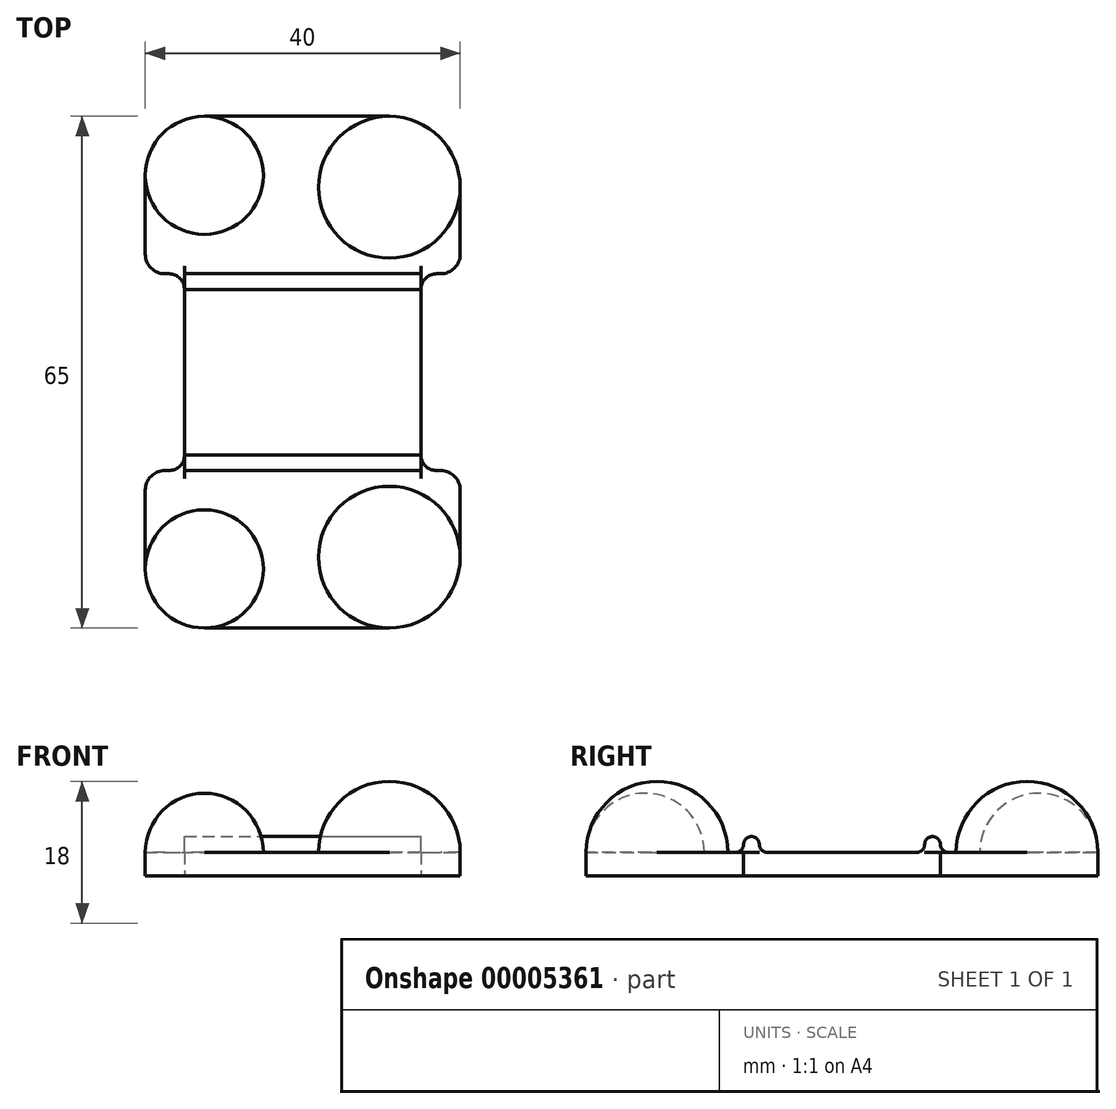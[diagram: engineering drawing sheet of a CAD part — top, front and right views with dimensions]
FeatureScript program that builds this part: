
annotation { "Feature Type Name" : "Feature", "Feature Type Description" : "" }
export const myFeature = defineFeature(function(context is Context, id is Id, definition is map)
    precondition{}
    {
        {
            var Q0;
            Q0=qCreatedBy(makeId("Top.planeOp"),FACE);
            var sketch = newSketch(context, id + "F0", { "sketchPlane" : qUnion([Q0])});
            skLineSegment(sketch, "E0.rect.bottom", {"start": v(20, 32.5) * mm, "end": v(-20, 32.5) * mm});
            skLineSegment(sketch, "E0.rect.top", {"start": v(20, -32.5) * mm, "end": v(-20, -32.5) * mm});
            skLineSegment(sketch, "E0.rect.left", {"start": v(20, 32.5) * mm, "end": v(20, -32.5) * mm});
            skLineSegment(sketch, "E0.rect.right", {"start": v(-20, 32.5) * mm, "end": v(-20, -32.5) * mm});
            skPoint(sketch, "E0.rect.middle", {"position": v(0, 0) * mm});
            skLineSegment(sketch, "E1", {"start": v(-20, 10.5) * mm, "end": v(20, 10.5) * mm});
            skLineSegment(sketch, "E2", {"start": v(-20, 12.5) * mm, "end": v(20, 12.5) * mm});
            skLineSegment(sketch, "E3", {"start": v(-20, -10.5) * mm, "end": v(20, -10.5) * mm});
            skLineSegment(sketch, "E4", {"start": v(-20, -12.5) * mm, "end": v(20, -12.5) * mm});
            skLineSegment(sketch, "E5", {"start": v(-15, 12.5) * mm, "end": v(-15, -12.5) * mm});
            skLineSegment(sketch, "E6", {"start": v(15, 12.5) * mm, "end": v(15, -12.5) * mm});
            skSolve(sketch);
        }
        {
            var Q0;
            Q0=makeQuery(id+"F0.imprint","IMPRINT",FACE,{"disambiguationData":[TD([[makeQuery(id+"F0.imprint","IMPRINT",EDGE,{"derivedFrom":sQuery(id+"F0.wireOp",EDGE,"E0.rect.bottom")}),1.0]])]});
            var Q1;
            Q1=makeQuery(id+"F0.imprint","IMPRINT",FACE,{"disambiguationData":[TD([[makeQuery(id+"F0.imprint","IMPRINT",EDGE,{"derivedFrom":sQuery(id+"F0.wireOp",EDGE,"bcf83515-ba27-4b76-bd59-bfaced73eee4.0")}),1.0]])]});
            var Q2;
            Q2=makeQuery(id+"F0.imprint","IMPRINT",FACE,{"disambiguationData":[TD([[makeQuery(id+"F0.imprint","IMPRINT",EDGE,{"derivedFrom":sQuery(id+"F0.wireOp",EDGE,"f3534231-453a-4a65-ba47-b9244893f894.bottom")}),1.0]])]});
            var Q3;
            Q3=makeQuery(id+"F0.imprint","IMPRINT",FACE,{"disambiguationData":[TD([[makeQuery(id+"F0.imprint","IMPRINT",EDGE,{"derivedFrom":sQuery(id+"F0.wireOp",EDGE,"e6d423b5-386a-40f2-9fc6-510d5bb70e3d.right")}),-1.0]])]});
            var Q4;
            Q4=makeQuery(id+"F0.imprint","IMPRINT",FACE,{"disambiguationData":[TD([[makeQuery(id+"F0.imprint","IMPRINT",EDGE,{"derivedFrom":sQuery(id+"F0.wireOp",EDGE,"a5c94823-2199-42b4-8307-fa219b560c5c0.MirrorCS")}),1.0]])]});
            var Q5;
            {var subQ2=sQuery(id+"F0.wireOp",EDGE,"E0.rect.top");Q5=makeQuery(id+"F0.imprint","IMPRINT",FACE,{"disambiguationData":[TD([[makeQuery(id+"F0.imprint","IMPRINT",EDGE,{"derivedFrom":subQ2}),-1.0]])]});}
            var Q6;
            {var subQ0=sQuery(id+"F0.wireOp",EDGE,"E5");var subQ1=sQuery(id+"F0.wireOp",EDGE,"E3");var subQ2=makeQuery(id+"F0.imprint","INTERSECT",VERTEX,{"derivedFrom":[subQ1,subQ0]});Q6=makeQuery(id+"F0.imprint","IMPRINT",FACE,{"disambiguationData":[TD([[makeQuery(id+"F0.imprint","IMPRINT",EDGE,{"disambiguationData":[TD([[subQ2,-1.0]])],"derivedFrom":subQ1}),-1.0]])]});}
            var Q7;
            {var subQ0=sQuery(id+"F0.wireOp",EDGE,"E5");var subQ1=sQuery(id+"F0.wireOp",EDGE,"E1");var subQ2=makeQuery(id+"F0.imprint","INTERSECT",VERTEX,{"derivedFrom":[subQ1,subQ0]});Q7=makeQuery(id+"F0.imprint","IMPRINT",FACE,{"disambiguationData":[TD([[makeQuery(id+"F0.imprint","IMPRINT",EDGE,{"disambiguationData":[TD([[subQ2,-1.0]])],"derivedFrom":subQ1}),-1.0]])]});}
            var Q8;
            {var subQ0=sQuery(id+"F0.wireOp",EDGE,"E5");var subQ1=sQuery(id+"F0.wireOp",EDGE,"E1");var subQ2=makeQuery(id+"F0.imprint","INTERSECT",VERTEX,{"derivedFrom":[subQ1,subQ0]});Q8=makeQuery(id+"F0.imprint","IMPRINT",FACE,{"disambiguationData":[TD([[makeQuery(id+"F0.imprint","IMPRINT",EDGE,{"disambiguationData":[TD([[subQ2,-1.0]])],"derivedFrom":subQ1}),1.0]])]});}
            extrude(context, id + "F1", {"entities" : qUnion([Q0, Q1, Q2, Q3, Q4, Q5, Q6, Q7, Q8]), "depth" : 3 * mm});
        }
        {
            var Q0;
            Q0=makeQuery(id+"F1.opExtrude","CAP_FACE",FACE,{"disambiguationData":[OSD([sQuery(id+"F0.wireOp",EDGE,"E0.rect.bottom"),sQuery(id+"F0.wireOp",EDGE,"E0.rect.top"),sQuery(id+"F0.wireOp",EDGE,"E0.rect.left"),sQuery(id+"F0.wireOp",EDGE,"E0.rect.right")])],"isStart":false});
            var sketch = newSketch(context, id + "F2", { "sketchPlane" : qUnion([Q0])});
            skCircle(sketch, "E7", {"center": v(-12.5, 25) * mm, "radius": 7.5 * mm});
            skLineSegment(sketch, "E8", {"start": v(-12.5, 32.5) * mm, "end": v(-12.5, 17.5) * mm});
            skCircle(sketch, "E9", {"center": v(11, 23.5) * mm, "radius": 9 * mm});
            skCircle(sketch, "E10", {"center": v(-12.5, -25) * mm, "radius": 7.5 * mm});
            skCircle(sketch, "E11", {"center": v(11, -23.5) * mm, "radius": 9 * mm});
            skLineSegment(sketch, "E12", {"start": v(-12.5, -17.5) * mm, "end": v(-12.5, -32.5) * mm});
            skLineSegment(sketch, "E13", {"start": v(11, -14.5) * mm, "end": v(11, -32.5) * mm});
            skLineSegment(sketch, "E14", {"start": v(11, 14.5) * mm, "end": v(11, 32.5) * mm});
            skSolve(sketch);
        }
        {
            var Q0;
            {var subQ0=sQuery(id+"F2.wireOp",EDGE,"E8");Q0=makeQuery(id+"F2.imprint","IMPRINT",FACE,{"disambiguationData":[TD([[makeQuery(id+"F2.imprint","IMPRINT",EDGE,{"derivedFrom":subQ0}),-1.0]])]});}
            var Q1;
            Q1=sQuery(id+"F2.wireOp",EDGE,"E8");
            revolve(context, id + "F3", {"operationType" : NewBodyOperationType.ADD, "entities" : qUnion([Q0]), "axis" : qUnion([Q1]), "revolveType" : RevolveType.ONE_DIRECTION, "oppositeDirection" : true, "angle" : 180 * degree});
        }
        {
            var Q0;
            {var subQ0=sQuery(id+"F2.wireOp",EDGE,"E14");Q0=makeQuery(id+"F2.imprint","IMPRINT",FACE,{"disambiguationData":[TD([[makeQuery(id+"F2.imprint","IMPRINT",EDGE,{"derivedFrom":subQ0}),1.0]])]});}
            var Q1;
            Q1=sQuery(id+"F2.wireOp",EDGE,"E14");
            revolve(context, id + "F4", {"operationType" : NewBodyOperationType.ADD, "entities" : qUnion([Q0]), "axis" : qUnion([Q1]), "revolveType" : RevolveType.ONE_DIRECTION, "angle" : 180 * degree});
        }
        {
            var Q0;
            {var subQ0=sQuery(id+"F2.wireOp",EDGE,"E12");Q0=makeQuery(id+"F2.imprint","IMPRINT",FACE,{"disambiguationData":[TD([[makeQuery(id+"F2.imprint","IMPRINT",EDGE,{"derivedFrom":subQ0}),-1.0]])]});}
            var Q1;
            Q1=sQuery(id+"F2.wireOp",EDGE,"E12");
            revolve(context, id + "F5", {"operationType" : NewBodyOperationType.ADD, "entities" : qUnion([Q0]), "axis" : qUnion([Q1]), "revolveType" : RevolveType.ONE_DIRECTION, "oppositeDirection" : true, "angle" : 180 * degree});
        }
        {
            var Q0;
            {var subQ0=sQuery(id+"F2.wireOp",EDGE,"E13");Q0=makeQuery(id+"F2.imprint","IMPRINT",FACE,{"disambiguationData":[TD([[makeQuery(id+"F2.imprint","IMPRINT",EDGE,{"derivedFrom":subQ0}),-1.0]])]});}
            var Q1;
            Q1=sQuery(id+"F2.wireOp",EDGE,"E13");
            revolve(context, id + "F6", {"operationType" : NewBodyOperationType.ADD, "entities" : qUnion([Q0]), "axis" : qUnion([Q1]), "revolveType" : RevolveType.ONE_DIRECTION, "oppositeDirection" : true, "angle" : 180 * degree});
        }
        {
            var Q0;
            {var subQ0=sQuery(id+"F2.wireOp",EDGE,"E11");var subQ1=sQuery(id+"F0.wireOp",EDGE,"E0.rect.top");var subQ2=makeQuery(id+"F1.opExtrude","CAP_EDGE",EDGE,{"disambiguationData":[OSD([subQ1])],"isStart":false});var subQ3=makeQuery(id+"F2.imprint","INTERSECT",VERTEX,{"derivedFrom":[subQ2,subQ0,sQuery(id+"F2.wireOp",EDGE,"E13")]});Q0=makeQuery(id+"F2.imprint","IMPRINT",FACE,{"disambiguationData":[TD([[makeQuery(id+"F2.imprint","IMPRINT",EDGE,{"disambiguationData":[TD([[subQ3,-1.0]])],"derivedFrom":subQ0}),-1.0]])]});}
            var Q1;
            {var subQ0=sQuery(id+"F2.wireOp",EDGE,"E10");var subQ1=sQuery(id+"F0.wireOp",EDGE,"E0.rect.top");var subQ2=makeQuery(id+"F1.opExtrude","CAP_EDGE",EDGE,{"disambiguationData":[OSD([subQ1])],"isStart":false});var subQ3=makeQuery(id+"F2.imprint","INTERSECT",VERTEX,{"derivedFrom":[subQ2,subQ0,sQuery(id+"F2.wireOp",EDGE,"E12")]});Q1=makeQuery(id+"F2.imprint","IMPRINT",FACE,{"disambiguationData":[TD([[makeQuery(id+"F2.imprint","IMPRINT",EDGE,{"disambiguationData":[TD([[subQ3,1.0]])],"derivedFrom":subQ0}),-1.0]])]});}
            var Q2;
            {var subQ0=sQuery(id+"F2.wireOp",EDGE,"E7");var subQ1=sQuery(id+"F0.wireOp",EDGE,"E0.rect.bottom");var subQ2=makeQuery(id+"F1.opExtrude","CAP_EDGE",EDGE,{"disambiguationData":[OSD([subQ1])],"isStart":false});var subQ3=makeQuery(id+"F2.imprint","INTERSECT",VERTEX,{"derivedFrom":[subQ2,sQuery(id+"F2.wireOp",EDGE,"E8"),subQ0]});Q2=makeQuery(id+"F2.imprint","IMPRINT",FACE,{"disambiguationData":[TD([[makeQuery(id+"F2.imprint","IMPRINT",EDGE,{"disambiguationData":[TD([[subQ3,-1.0]])],"derivedFrom":subQ0}),-1.0]])]});}
            var Q3;
            {var subQ0=sQuery(id+"F2.wireOp",EDGE,"E9");var subQ1=sQuery(id+"F0.wireOp",EDGE,"E0.rect.bottom");var subQ2=makeQuery(id+"F1.opExtrude","CAP_EDGE",EDGE,{"disambiguationData":[OSD([subQ1])],"isStart":false});var subQ3=makeQuery(id+"F2.imprint","INTERSECT",VERTEX,{"derivedFrom":[subQ2,subQ0,sQuery(id+"F2.wireOp",EDGE,"E14")]});Q3=makeQuery(id+"F2.imprint","IMPRINT",FACE,{"disambiguationData":[TD([[makeQuery(id+"F2.imprint","IMPRINT",EDGE,{"disambiguationData":[TD([[subQ3,1.0]])],"derivedFrom":subQ0}),-1.0]])]});}
            extrude(context, id + "F7", {"entities" : qUnion([Q0, Q1, Q2, Q3]), "operationType" : NewBodyOperationType.REMOVE, "oppositeDirection" : true, "depth" : 5 * mm});
        }
        {
            var Q0;
            Q0=makeQuery(id+"F1.opExtrude","SWEPT_EDGE",EDGE,{"disambiguationData":[OSD([sQuery(id+"F0.wireOp",EDGE,"E0.rect.left"),sQuery(id+"F0.wireOp",EDGE,"a298e613-06a3-4d8a-99ce-b2c4759a3d300.MirrorCS")])]});
            var Q1;
            Q1=makeQuery(id+"F1.opExtrude","SWEPT_EDGE",EDGE,{"disambiguationData":[OSD([sQuery(id+"F0.wireOp",EDGE,"E0.rect.left"),sQuery(id+"F0.wireOp",EDGE,"a298e613-06a3-4d8a-99ce-b2c4759a3d301.MirrorCS")])]});
            var Q2;
            Q2=makeQuery(id+"F1.opExtrude","SWEPT_EDGE",EDGE,{"disambiguationData":[OSD([sQuery(id+"F0.wireOp",EDGE,"a298e613-06a3-4d8a-99ce-b2c4759a3d301.MirrorCS"),sQuery(id+"F0.wireOp",EDGE,"a298e613-06a3-4d8a-99ce-b2c4759a3d302.MirrorCS")])]});
            var Q3;
            Q3=makeQuery(id+"F1.opExtrude","SWEPT_EDGE",EDGE,{"disambiguationData":[OSD([sQuery(id+"F0.wireOp",EDGE,"a298e613-06a3-4d8a-99ce-b2c4759a3d300.MirrorCS"),sQuery(id+"F0.wireOp",EDGE,"a298e613-06a3-4d8a-99ce-b2c4759a3d302.MirrorCS")])]});
            var Q4;
            Q4=makeQuery(id+"F1.opExtrude","SWEPT_EDGE",EDGE,{"disambiguationData":[OSD([sQuery(id+"F0.wireOp",EDGE,"E0.rect.right"),sQuery(id+"F0.wireOp",EDGE,"e6d423b5-386a-40f2-9fc6-510d5bb70e3d.top"),sQuery(id+"F0.wireOp",EDGE,"e6d423b5-386a-40f2-9fc6-510d5bb70e3d.left")])]});
            var Q5;
            Q5=makeQuery(id+"F1.opExtrude","SWEPT_EDGE",EDGE,{"disambiguationData":[OSD([sQuery(id+"F0.wireOp",EDGE,"e6d423b5-386a-40f2-9fc6-510d5bb70e3d.top"),sQuery(id+"F0.wireOp",EDGE,"e6d423b5-386a-40f2-9fc6-510d5bb70e3d.right")])]});
            var Q6;
            Q6=makeQuery(id+"F1.opExtrude","SWEPT_EDGE",EDGE,{"disambiguationData":[OSD([sQuery(id+"F0.wireOp",EDGE,"E0.rect.right"),sQuery(id+"F0.wireOp",EDGE,"e6d423b5-386a-40f2-9fc6-510d5bb70e3d.bottom"),sQuery(id+"F0.wireOp",EDGE,"e6d423b5-386a-40f2-9fc6-510d5bb70e3d.left")])]});
            var Q7;
            Q7=makeQuery(id+"F1.opExtrude","SWEPT_EDGE",EDGE,{"disambiguationData":[OSD([sQuery(id+"F0.wireOp",EDGE,"e6d423b5-386a-40f2-9fc6-510d5bb70e3d.bottom"),sQuery(id+"F0.wireOp",EDGE,"e6d423b5-386a-40f2-9fc6-510d5bb70e3d.right")])]});
            fillet(context, id + "F8", {"entities" : qUnion([Q0, Q1, Q2, Q3, Q4, Q5, Q6, Q7]), "radius" : 2.5 * mm, "tangentPropagation" : true, "allowEdgeOverflow" : false});
        }
        {
            var Q0;
            Q0=makeQuery(id+"F1.opExtrude","SWEPT_EDGE",EDGE,{"disambiguationData":[OSD([sQuery(id+"F0.wireOp",EDGE,"E2"),sQuery(id+"F0.wireOp",EDGE,"E5")])]});
            var Q1;
            Q1=makeQuery(id+"F1.opExtrude","SWEPT_EDGE",EDGE,{"disambiguationData":[OSD([sQuery(id+"F0.wireOp",EDGE,"E4"),sQuery(id+"F0.wireOp",EDGE,"E5")])]});
            var Q2;
            Q2=makeQuery(id+"F1.opExtrude","SWEPT_EDGE",EDGE,{"disambiguationData":[OSD([sQuery(id+"F0.wireOp",EDGE,"E4"),sQuery(id+"F0.wireOp",EDGE,"E6")])]});
            var Q3;
            Q3=makeQuery(id+"F1.opExtrude","SWEPT_EDGE",EDGE,{"disambiguationData":[OSD([sQuery(id+"F0.wireOp",EDGE,"E2"),sQuery(id+"F0.wireOp",EDGE,"E6")])]});
            fillet(context, id + "F9", {"entities" : qUnion([Q0, Q1, Q2, Q3]), "radius" : 2 * mm, "tangentPropagation" : true, "allowEdgeOverflow" : false});
        }
        {
            var Q0;
            {var subQ0=sQuery(id+"F0.wireOp",EDGE,"E5");var subQ1=sQuery(id+"F0.wireOp",EDGE,"E3");var subQ2=makeQuery(id+"F0.imprint","INTERSECT",VERTEX,{"derivedFrom":[subQ1,subQ0]});Q0=makeQuery(id+"F0.imprint","IMPRINT",FACE,{"disambiguationData":[TD([[makeQuery(id+"F0.imprint","IMPRINT",EDGE,{"disambiguationData":[TD([[subQ2,-1.0]])],"derivedFrom":subQ1}),-1.0]])]});}
            var Q1;
            {var subQ0=sQuery(id+"F0.wireOp",EDGE,"E5");var subQ1=sQuery(id+"F0.wireOp",EDGE,"E1");var subQ2=makeQuery(id+"F0.imprint","INTERSECT",VERTEX,{"derivedFrom":[subQ1,subQ0]});Q1=makeQuery(id+"F0.imprint","IMPRINT",FACE,{"disambiguationData":[TD([[makeQuery(id+"F0.imprint","IMPRINT",EDGE,{"disambiguationData":[TD([[subQ2,-1.0]])],"derivedFrom":subQ1}),1.0]])]});}
            extrude(context, id + "F10", {"entities" : qUnion([Q0, Q1]), "operationType" : NewBodyOperationType.ADD, "depth" : 5 * mm});
        }
        {
            var Q0;
            {var subQ0=sQuery(id+"F0.wireOp",EDGE,"E2");var subQ1=sQuery(id+"F0.wireOp",EDGE,"E4");var subQ2=sQuery(id+"F0.wireOp",EDGE,"E0.rect.right");var subQ3=makeQuery(id+"F0.imprint","INTERSECT",VERTEX,{"derivedFrom":[subQ2,subQ1]});var subQ4=sQuery(id+"F0.wireOp",EDGE,"E5");var subQ5=makeQuery(id+"F1.opExtrude","SWEPT_FACE",FACE,{"disambiguationData":[OSD([subQ1]),TDD([makeQuery(id+"F0.imprint","IMPRINT",EDGE,{"disambiguationData":[TD([[subQ3,-1.0]])],"derivedFrom":subQ1})])]});var subQ6=sQuery(id+"F0.wireOp",EDGE,"E0.rect.left");var subQ7=makeQuery(id+"F0.imprint","INTERSECT",VERTEX,{"derivedFrom":[subQ6,subQ0]});var subQ8=sQuery(id+"F0.wireOp",EDGE,"E6");var subQ9=makeQuery(id+"F1.opExtrude","SWEPT_FACE",FACE,{"disambiguationData":[OSD([subQ0]),TDD([makeQuery(id+"F0.imprint","IMPRINT",EDGE,{"disambiguationData":[TD([[subQ7,1.0]])],"derivedFrom":subQ0})])]});var subQ10=makeQuery(id+"F0.imprint","INTERSECT",VERTEX,{"derivedFrom":[subQ2,subQ0]});var subQ11=makeQuery(id+"F1.opExtrude","SWEPT_FACE",FACE,{"disambiguationData":[OSD([subQ0]),TDD([makeQuery(id+"F0.imprint","IMPRINT",EDGE,{"disambiguationData":[TD([[subQ10,-1.0]])],"derivedFrom":subQ0})])]});var subQ12=sQuery(id+"F0.wireOp",EDGE,"E0.rect.top");var subQ13=makeQuery(id+"F1.opExtrude","SWEPT_FACE",FACE,{"disambiguationData":[OSD([subQ2]),TDD([makeQuery(id+"F0.imprint","IMPRINT",EDGE,{"disambiguationData":[TD([[makeQuery(id+"F0.imprint","INTERSECT",VERTEX,{"derivedFrom":[subQ12,subQ2]}),1.0]])],"derivedFrom":subQ2})])]});var subQ14=sQuery(id+"F0.wireOp",EDGE,"E0.rect.bottom");var subQ15=makeQuery(id+"F1.opExtrude","SWEPT_FACE",FACE,{"disambiguationData":[OSD([subQ2]),TDD([makeQuery(id+"F0.imprint","IMPRINT",EDGE,{"disambiguationData":[TD([[makeQuery(id+"F0.imprint","INTERSECT",VERTEX,{"derivedFrom":[subQ14,subQ2]}),-1.0]])],"derivedFrom":subQ2})])]});var subQ16=makeQuery(id+"F0.imprint","INTERSECT",VERTEX,{"derivedFrom":[subQ6,subQ1]});var subQ17=makeQuery(id+"F1.opExtrude","SWEPT_FACE",FACE,{"disambiguationData":[OSD([subQ6]),TDD([makeQuery(id+"F0.imprint","IMPRINT",EDGE,{"disambiguationData":[TD([[makeQuery(id+"F0.imprint","INTERSECT",VERTEX,{"derivedFrom":[subQ12,subQ6]}),1.0]])],"derivedFrom":subQ6})])]});var subQ18=makeQuery(id+"F3.opRevolve","SWEPT_FACE",FACE,{"disambiguationData":[OSD([sQuery(id+"F2.wireOp",EDGE,"E7")])]});var subQ19=makeQuery(id+"F1.opExtrude","SWEPT_FACE",FACE,{"disambiguationData":[OSD([subQ14])]});var subQ20=makeQuery(id+"F1.opExtrude","CAP_FACE",FACE,{"disambiguationData":[OSD([subQ14,subQ12,subQ6,subQ2,subQ0,subQ1,subQ4,subQ8])],"isStart":false});var subQ21=makeQuery(id+"F1.opExtrude","SWEPT_FACE",FACE,{"disambiguationData":[OSD([subQ12])]});var subQ22=makeQuery(id+"F1.opExtrude","SWEPT_FACE",FACE,{"disambiguationData":[OSD([subQ6]),TDD([makeQuery(id+"F0.imprint","IMPRINT",EDGE,{"disambiguationData":[TD([[makeQuery(id+"F0.imprint","INTERSECT",VERTEX,{"derivedFrom":[subQ14,subQ6]}),-1.0]])],"derivedFrom":subQ6})])]});var subQ23=makeQuery(id+"F1.opExtrude","SWEPT_FACE",FACE,{"disambiguationData":[OSD([subQ1]),TDD([makeQuery(id+"F0.imprint","IMPRINT",EDGE,{"disambiguationData":[TD([[subQ16,1.0]])],"derivedFrom":subQ1})])]});var subQ24=makeQuery(id+"F1.opExtrude","SWEPT_FACE",FACE,{"disambiguationData":[OSD([subQ4])]});var subQ25=makeQuery(id+"F1.opExtrude","SWEPT_FACE",FACE,{"disambiguationData":[OSD([subQ8])]});var subQ26=makeQuery(id+"F4.opRevolve","SWEPT_FACE",FACE,{"disambiguationData":[OSD([sQuery(id+"F2.wireOp",EDGE,"E9")])]});var subQ27=makeQuery(id+"F5.opRevolve","SWEPT_FACE",FACE,{"disambiguationData":[OSD([sQuery(id+"F2.wireOp",EDGE,"E10")])]});Q0=makeQuery(id+"F10.boolean.opBoolean","INTERSECT",EDGE,{"derivedFrom":[makeQuery(id+"F6.boolean.opBoolean","SPLIT",FACE,{"disambiguationData":[TD([subQ19,subQ20,subQ21,subQ22,subQ17,subQ15,subQ13,subQ11,subQ9,subQ5,subQ23,subQ24,subQ25,subQ18,subQ26,subQ27,makeQuery(id+"F6.opRevolve","SWEPT_FACE",FACE,{"disambiguationData":[OSD([sQuery(id+"F2.wireOp",EDGE,"E11")])]})])],"derivedFrom":makeQuery(id+"F5.boolean.opBoolean","SPLIT",FACE,{"disambiguationData":[TD([subQ19,subQ20,subQ21,subQ22,subQ17,subQ15,subQ13,subQ11,subQ9,subQ5,subQ23,subQ24,subQ25,subQ18,subQ26,subQ27])],"derivedFrom":makeQuery(id+"F4.boolean.opBoolean","SPLIT",FACE,{"disambiguationData":[TD([subQ19,subQ20,subQ21,subQ22,subQ17,subQ15,subQ13,subQ11,subQ9,subQ5,subQ23,subQ24,subQ25,subQ18,subQ26])],"derivedFrom":makeQuery(id+"F3.boolean.opBoolean","SPLIT",FACE,{"disambiguationData":[TD([subQ19,subQ20,subQ21,subQ22,subQ17,subQ15,subQ13,subQ11,subQ9,subQ5,subQ23,subQ24,subQ25,subQ18])],"derivedFrom":subQ20})})})}),makeQuery(id+"F10.opExtrude","SWEPT_FACE",FACE,{"disambiguationData":[OSD([subQ0])]})]});}
            var Q1;
            Q1=makeQuery(id+"F10.opExtrude","CAP_EDGE",EDGE,{"disambiguationData":[OSD([sQuery(id+"F0.wireOp",EDGE,"E2")])],"isStart":false});
            var Q2;
            Q2=makeQuery(id+"F10.opExtrude","CAP_EDGE",EDGE,{"disambiguationData":[OSD([sQuery(id+"F0.wireOp",EDGE,"E1")])],"isStart":false});
            var Q3;
            {var subQ0=sQuery(id+"F0.wireOp",EDGE,"E4");var subQ1=sQuery(id+"F0.wireOp",EDGE,"E0.rect.right");var subQ2=makeQuery(id+"F0.imprint","INTERSECT",VERTEX,{"derivedFrom":[subQ1,subQ0]});var subQ3=sQuery(id+"F0.wireOp",EDGE,"E5");var subQ4=makeQuery(id+"F1.opExtrude","SWEPT_FACE",FACE,{"disambiguationData":[OSD([subQ0]),TDD([makeQuery(id+"F0.imprint","IMPRINT",EDGE,{"disambiguationData":[TD([[subQ2,-1.0]])],"derivedFrom":subQ0})])]});var subQ5=sQuery(id+"F0.wireOp",EDGE,"E2");var subQ6=sQuery(id+"F0.wireOp",EDGE,"E0.rect.left");var subQ7=makeQuery(id+"F0.imprint","INTERSECT",VERTEX,{"derivedFrom":[subQ6,subQ5]});var subQ8=sQuery(id+"F0.wireOp",EDGE,"E6");var subQ9=makeQuery(id+"F1.opExtrude","SWEPT_FACE",FACE,{"disambiguationData":[OSD([subQ5]),TDD([makeQuery(id+"F0.imprint","IMPRINT",EDGE,{"disambiguationData":[TD([[subQ7,1.0]])],"derivedFrom":subQ5})])]});var subQ10=makeQuery(id+"F0.imprint","INTERSECT",VERTEX,{"derivedFrom":[subQ1,subQ5]});var subQ11=makeQuery(id+"F1.opExtrude","SWEPT_FACE",FACE,{"disambiguationData":[OSD([subQ5]),TDD([makeQuery(id+"F0.imprint","IMPRINT",EDGE,{"disambiguationData":[TD([[subQ10,-1.0]])],"derivedFrom":subQ5})])]});var subQ12=sQuery(id+"F0.wireOp",EDGE,"E0.rect.top");var subQ13=makeQuery(id+"F1.opExtrude","SWEPT_FACE",FACE,{"disambiguationData":[OSD([subQ1]),TDD([makeQuery(id+"F0.imprint","IMPRINT",EDGE,{"disambiguationData":[TD([[makeQuery(id+"F0.imprint","INTERSECT",VERTEX,{"derivedFrom":[subQ12,subQ1]}),1.0]])],"derivedFrom":subQ1})])]});var subQ14=sQuery(id+"F0.wireOp",EDGE,"E0.rect.bottom");var subQ15=makeQuery(id+"F1.opExtrude","SWEPT_FACE",FACE,{"disambiguationData":[OSD([subQ1]),TDD([makeQuery(id+"F0.imprint","IMPRINT",EDGE,{"disambiguationData":[TD([[makeQuery(id+"F0.imprint","INTERSECT",VERTEX,{"derivedFrom":[subQ14,subQ1]}),-1.0]])],"derivedFrom":subQ1})])]});var subQ16=makeQuery(id+"F0.imprint","INTERSECT",VERTEX,{"derivedFrom":[subQ6,subQ0]});var subQ17=makeQuery(id+"F1.opExtrude","SWEPT_FACE",FACE,{"disambiguationData":[OSD([subQ6]),TDD([makeQuery(id+"F0.imprint","IMPRINT",EDGE,{"disambiguationData":[TD([[makeQuery(id+"F0.imprint","INTERSECT",VERTEX,{"derivedFrom":[subQ12,subQ6]}),1.0]])],"derivedFrom":subQ6})])]});var subQ18=makeQuery(id+"F3.opRevolve","SWEPT_FACE",FACE,{"disambiguationData":[OSD([sQuery(id+"F2.wireOp",EDGE,"E7")])]});var subQ19=makeQuery(id+"F1.opExtrude","SWEPT_FACE",FACE,{"disambiguationData":[OSD([subQ14])]});var subQ20=makeQuery(id+"F1.opExtrude","CAP_FACE",FACE,{"disambiguationData":[OSD([subQ14,subQ12,subQ6,subQ1,subQ5,subQ0,subQ3,subQ8])],"isStart":false});var subQ21=makeQuery(id+"F1.opExtrude","SWEPT_FACE",FACE,{"disambiguationData":[OSD([subQ12])]});var subQ22=makeQuery(id+"F1.opExtrude","SWEPT_FACE",FACE,{"disambiguationData":[OSD([subQ6]),TDD([makeQuery(id+"F0.imprint","IMPRINT",EDGE,{"disambiguationData":[TD([[makeQuery(id+"F0.imprint","INTERSECT",VERTEX,{"derivedFrom":[subQ14,subQ6]}),-1.0]])],"derivedFrom":subQ6})])]});var subQ23=makeQuery(id+"F1.opExtrude","SWEPT_FACE",FACE,{"disambiguationData":[OSD([subQ0]),TDD([makeQuery(id+"F0.imprint","IMPRINT",EDGE,{"disambiguationData":[TD([[subQ16,1.0]])],"derivedFrom":subQ0})])]});var subQ24=makeQuery(id+"F1.opExtrude","SWEPT_FACE",FACE,{"disambiguationData":[OSD([subQ3])]});var subQ25=makeQuery(id+"F1.opExtrude","SWEPT_FACE",FACE,{"disambiguationData":[OSD([subQ8])]});var subQ26=makeQuery(id+"F4.opRevolve","SWEPT_FACE",FACE,{"disambiguationData":[OSD([sQuery(id+"F2.wireOp",EDGE,"E9")])]});var subQ27=makeQuery(id+"F5.opRevolve","SWEPT_FACE",FACE,{"disambiguationData":[OSD([sQuery(id+"F2.wireOp",EDGE,"E10")])]});Q3=makeQuery(id+"F10.boolean.opBoolean","INTERSECT",EDGE,{"derivedFrom":[makeQuery(id+"F6.boolean.opBoolean","SPLIT",FACE,{"disambiguationData":[TD([subQ19,subQ20,subQ21,subQ22,subQ17,subQ15,subQ13,subQ11,subQ9,subQ4,subQ23,subQ24,subQ25,subQ18,subQ26,subQ27,makeQuery(id+"F6.opRevolve","SWEPT_FACE",FACE,{"disambiguationData":[OSD([sQuery(id+"F2.wireOp",EDGE,"E11")])]})])],"derivedFrom":makeQuery(id+"F5.boolean.opBoolean","SPLIT",FACE,{"disambiguationData":[TD([subQ19,subQ20,subQ21,subQ22,subQ17,subQ15,subQ13,subQ11,subQ9,subQ4,subQ23,subQ24,subQ25,subQ18,subQ26,subQ27])],"derivedFrom":makeQuery(id+"F4.boolean.opBoolean","SPLIT",FACE,{"disambiguationData":[TD([subQ19,subQ20,subQ21,subQ22,subQ17,subQ15,subQ13,subQ11,subQ9,subQ4,subQ23,subQ24,subQ25,subQ18,subQ26])],"derivedFrom":makeQuery(id+"F3.boolean.opBoolean","SPLIT",FACE,{"disambiguationData":[TD([subQ19,subQ20,subQ21,subQ22,subQ17,subQ15,subQ13,subQ11,subQ9,subQ4,subQ23,subQ24,subQ25,subQ18])],"derivedFrom":subQ20})})})}),makeQuery(id+"F10.opExtrude","SWEPT_FACE",FACE,{"disambiguationData":[OSD([sQuery(id+"F0.wireOp",EDGE,"E1")])]})]});}
            var Q4;
            {var subQ0=sQuery(id+"F0.wireOp",EDGE,"E4");var subQ1=sQuery(id+"F0.wireOp",EDGE,"E0.rect.right");var subQ2=makeQuery(id+"F0.imprint","INTERSECT",VERTEX,{"derivedFrom":[subQ1,subQ0]});var subQ3=sQuery(id+"F0.wireOp",EDGE,"E5");var subQ4=makeQuery(id+"F1.opExtrude","SWEPT_FACE",FACE,{"disambiguationData":[OSD([subQ0]),TDD([makeQuery(id+"F0.imprint","IMPRINT",EDGE,{"disambiguationData":[TD([[subQ2,-1.0]])],"derivedFrom":subQ0})])]});var subQ5=sQuery(id+"F0.wireOp",EDGE,"E2");var subQ6=sQuery(id+"F0.wireOp",EDGE,"E0.rect.left");var subQ7=makeQuery(id+"F0.imprint","INTERSECT",VERTEX,{"derivedFrom":[subQ6,subQ5]});var subQ8=sQuery(id+"F0.wireOp",EDGE,"E6");var subQ9=makeQuery(id+"F1.opExtrude","SWEPT_FACE",FACE,{"disambiguationData":[OSD([subQ5]),TDD([makeQuery(id+"F0.imprint","IMPRINT",EDGE,{"disambiguationData":[TD([[subQ7,1.0]])],"derivedFrom":subQ5})])]});var subQ10=makeQuery(id+"F0.imprint","INTERSECT",VERTEX,{"derivedFrom":[subQ1,subQ5]});var subQ11=makeQuery(id+"F1.opExtrude","SWEPT_FACE",FACE,{"disambiguationData":[OSD([subQ5]),TDD([makeQuery(id+"F0.imprint","IMPRINT",EDGE,{"disambiguationData":[TD([[subQ10,-1.0]])],"derivedFrom":subQ5})])]});var subQ12=sQuery(id+"F0.wireOp",EDGE,"E0.rect.top");var subQ13=makeQuery(id+"F1.opExtrude","SWEPT_FACE",FACE,{"disambiguationData":[OSD([subQ1]),TDD([makeQuery(id+"F0.imprint","IMPRINT",EDGE,{"disambiguationData":[TD([[makeQuery(id+"F0.imprint","INTERSECT",VERTEX,{"derivedFrom":[subQ12,subQ1]}),1.0]])],"derivedFrom":subQ1})])]});var subQ14=sQuery(id+"F0.wireOp",EDGE,"E0.rect.bottom");var subQ15=makeQuery(id+"F1.opExtrude","SWEPT_FACE",FACE,{"disambiguationData":[OSD([subQ1]),TDD([makeQuery(id+"F0.imprint","IMPRINT",EDGE,{"disambiguationData":[TD([[makeQuery(id+"F0.imprint","INTERSECT",VERTEX,{"derivedFrom":[subQ14,subQ1]}),-1.0]])],"derivedFrom":subQ1})])]});var subQ16=makeQuery(id+"F0.imprint","INTERSECT",VERTEX,{"derivedFrom":[subQ6,subQ0]});var subQ17=makeQuery(id+"F1.opExtrude","SWEPT_FACE",FACE,{"disambiguationData":[OSD([subQ6]),TDD([makeQuery(id+"F0.imprint","IMPRINT",EDGE,{"disambiguationData":[TD([[makeQuery(id+"F0.imprint","INTERSECT",VERTEX,{"derivedFrom":[subQ12,subQ6]}),1.0]])],"derivedFrom":subQ6})])]});var subQ18=makeQuery(id+"F3.opRevolve","SWEPT_FACE",FACE,{"disambiguationData":[OSD([sQuery(id+"F2.wireOp",EDGE,"E7")])]});var subQ19=makeQuery(id+"F1.opExtrude","SWEPT_FACE",FACE,{"disambiguationData":[OSD([subQ14])]});var subQ20=makeQuery(id+"F1.opExtrude","CAP_FACE",FACE,{"disambiguationData":[OSD([subQ14,subQ12,subQ6,subQ1,subQ5,subQ0,subQ3,subQ8])],"isStart":false});var subQ21=makeQuery(id+"F1.opExtrude","SWEPT_FACE",FACE,{"disambiguationData":[OSD([subQ12])]});var subQ22=makeQuery(id+"F1.opExtrude","SWEPT_FACE",FACE,{"disambiguationData":[OSD([subQ6]),TDD([makeQuery(id+"F0.imprint","IMPRINT",EDGE,{"disambiguationData":[TD([[makeQuery(id+"F0.imprint","INTERSECT",VERTEX,{"derivedFrom":[subQ14,subQ6]}),-1.0]])],"derivedFrom":subQ6})])]});var subQ23=makeQuery(id+"F1.opExtrude","SWEPT_FACE",FACE,{"disambiguationData":[OSD([subQ0]),TDD([makeQuery(id+"F0.imprint","IMPRINT",EDGE,{"disambiguationData":[TD([[subQ16,1.0]])],"derivedFrom":subQ0})])]});var subQ24=makeQuery(id+"F1.opExtrude","SWEPT_FACE",FACE,{"disambiguationData":[OSD([subQ3])]});var subQ25=makeQuery(id+"F1.opExtrude","SWEPT_FACE",FACE,{"disambiguationData":[OSD([subQ8])]});var subQ26=makeQuery(id+"F4.opRevolve","SWEPT_FACE",FACE,{"disambiguationData":[OSD([sQuery(id+"F2.wireOp",EDGE,"E9")])]});var subQ27=makeQuery(id+"F5.opRevolve","SWEPT_FACE",FACE,{"disambiguationData":[OSD([sQuery(id+"F2.wireOp",EDGE,"E10")])]});Q4=makeQuery(id+"F10.boolean.opBoolean","INTERSECT",EDGE,{"derivedFrom":[makeQuery(id+"F6.boolean.opBoolean","SPLIT",FACE,{"disambiguationData":[TD([subQ19,subQ20,subQ21,subQ22,subQ17,subQ15,subQ13,subQ11,subQ9,subQ4,subQ23,subQ24,subQ25,subQ18,subQ26,subQ27,makeQuery(id+"F6.opRevolve","SWEPT_FACE",FACE,{"disambiguationData":[OSD([sQuery(id+"F2.wireOp",EDGE,"E11")])]})])],"derivedFrom":makeQuery(id+"F5.boolean.opBoolean","SPLIT",FACE,{"disambiguationData":[TD([subQ19,subQ20,subQ21,subQ22,subQ17,subQ15,subQ13,subQ11,subQ9,subQ4,subQ23,subQ24,subQ25,subQ18,subQ26,subQ27])],"derivedFrom":makeQuery(id+"F4.boolean.opBoolean","SPLIT",FACE,{"disambiguationData":[TD([subQ19,subQ20,subQ21,subQ22,subQ17,subQ15,subQ13,subQ11,subQ9,subQ4,subQ23,subQ24,subQ25,subQ18,subQ26])],"derivedFrom":makeQuery(id+"F3.boolean.opBoolean","SPLIT",FACE,{"disambiguationData":[TD([subQ19,subQ20,subQ21,subQ22,subQ17,subQ15,subQ13,subQ11,subQ9,subQ4,subQ23,subQ24,subQ25,subQ18])],"derivedFrom":subQ20})})})}),makeQuery(id+"F10.opExtrude","SWEPT_FACE",FACE,{"disambiguationData":[OSD([sQuery(id+"F0.wireOp",EDGE,"E3")])]})]});}
            var Q5;
            Q5=makeQuery(id+"F10.opExtrude","CAP_EDGE",EDGE,{"disambiguationData":[OSD([sQuery(id+"F0.wireOp",EDGE,"E3")])],"isStart":false});
            var Q6;
            Q6=makeQuery(id+"F10.opExtrude","CAP_EDGE",EDGE,{"disambiguationData":[OSD([sQuery(id+"F0.wireOp",EDGE,"E4")])],"isStart":false});
            var Q7;
            {var subQ0=sQuery(id+"F0.wireOp",EDGE,"E4");var subQ1=sQuery(id+"F0.wireOp",EDGE,"E0.rect.right");var subQ2=makeQuery(id+"F0.imprint","INTERSECT",VERTEX,{"derivedFrom":[subQ1,subQ0]});var subQ3=sQuery(id+"F0.wireOp",EDGE,"E5");var subQ4=makeQuery(id+"F1.opExtrude","SWEPT_FACE",FACE,{"disambiguationData":[OSD([subQ0]),TDD([makeQuery(id+"F0.imprint","IMPRINT",EDGE,{"disambiguationData":[TD([[subQ2,-1.0]])],"derivedFrom":subQ0})])]});var subQ5=sQuery(id+"F0.wireOp",EDGE,"E2");var subQ6=sQuery(id+"F0.wireOp",EDGE,"E0.rect.left");var subQ7=makeQuery(id+"F0.imprint","INTERSECT",VERTEX,{"derivedFrom":[subQ6,subQ5]});var subQ8=sQuery(id+"F0.wireOp",EDGE,"E6");var subQ9=makeQuery(id+"F1.opExtrude","SWEPT_FACE",FACE,{"disambiguationData":[OSD([subQ5]),TDD([makeQuery(id+"F0.imprint","IMPRINT",EDGE,{"disambiguationData":[TD([[subQ7,1.0]])],"derivedFrom":subQ5})])]});var subQ10=makeQuery(id+"F0.imprint","INTERSECT",VERTEX,{"derivedFrom":[subQ1,subQ5]});var subQ11=makeQuery(id+"F1.opExtrude","SWEPT_FACE",FACE,{"disambiguationData":[OSD([subQ5]),TDD([makeQuery(id+"F0.imprint","IMPRINT",EDGE,{"disambiguationData":[TD([[subQ10,-1.0]])],"derivedFrom":subQ5})])]});var subQ12=sQuery(id+"F0.wireOp",EDGE,"E0.rect.top");var subQ13=makeQuery(id+"F1.opExtrude","SWEPT_FACE",FACE,{"disambiguationData":[OSD([subQ1]),TDD([makeQuery(id+"F0.imprint","IMPRINT",EDGE,{"disambiguationData":[TD([[makeQuery(id+"F0.imprint","INTERSECT",VERTEX,{"derivedFrom":[subQ12,subQ1]}),1.0]])],"derivedFrom":subQ1})])]});var subQ14=sQuery(id+"F0.wireOp",EDGE,"E0.rect.bottom");var subQ15=makeQuery(id+"F1.opExtrude","SWEPT_FACE",FACE,{"disambiguationData":[OSD([subQ1]),TDD([makeQuery(id+"F0.imprint","IMPRINT",EDGE,{"disambiguationData":[TD([[makeQuery(id+"F0.imprint","INTERSECT",VERTEX,{"derivedFrom":[subQ14,subQ1]}),-1.0]])],"derivedFrom":subQ1})])]});var subQ16=makeQuery(id+"F0.imprint","INTERSECT",VERTEX,{"derivedFrom":[subQ6,subQ0]});var subQ17=makeQuery(id+"F1.opExtrude","SWEPT_FACE",FACE,{"disambiguationData":[OSD([subQ6]),TDD([makeQuery(id+"F0.imprint","IMPRINT",EDGE,{"disambiguationData":[TD([[makeQuery(id+"F0.imprint","INTERSECT",VERTEX,{"derivedFrom":[subQ12,subQ6]}),1.0]])],"derivedFrom":subQ6})])]});var subQ18=makeQuery(id+"F3.opRevolve","SWEPT_FACE",FACE,{"disambiguationData":[OSD([sQuery(id+"F2.wireOp",EDGE,"E7")])]});var subQ19=makeQuery(id+"F1.opExtrude","SWEPT_FACE",FACE,{"disambiguationData":[OSD([subQ14])]});var subQ20=makeQuery(id+"F1.opExtrude","CAP_FACE",FACE,{"disambiguationData":[OSD([subQ14,subQ12,subQ6,subQ1,subQ5,subQ0,subQ3,subQ8])],"isStart":false});var subQ21=makeQuery(id+"F1.opExtrude","SWEPT_FACE",FACE,{"disambiguationData":[OSD([subQ12])]});var subQ22=makeQuery(id+"F1.opExtrude","SWEPT_FACE",FACE,{"disambiguationData":[OSD([subQ6]),TDD([makeQuery(id+"F0.imprint","IMPRINT",EDGE,{"disambiguationData":[TD([[makeQuery(id+"F0.imprint","INTERSECT",VERTEX,{"derivedFrom":[subQ14,subQ6]}),-1.0]])],"derivedFrom":subQ6})])]});var subQ23=makeQuery(id+"F1.opExtrude","SWEPT_FACE",FACE,{"disambiguationData":[OSD([subQ0]),TDD([makeQuery(id+"F0.imprint","IMPRINT",EDGE,{"disambiguationData":[TD([[subQ16,1.0]])],"derivedFrom":subQ0})])]});var subQ24=makeQuery(id+"F1.opExtrude","SWEPT_FACE",FACE,{"disambiguationData":[OSD([subQ3])]});var subQ25=makeQuery(id+"F1.opExtrude","SWEPT_FACE",FACE,{"disambiguationData":[OSD([subQ8])]});var subQ26=makeQuery(id+"F4.opRevolve","SWEPT_FACE",FACE,{"disambiguationData":[OSD([sQuery(id+"F2.wireOp",EDGE,"E9")])]});var subQ27=makeQuery(id+"F5.opRevolve","SWEPT_FACE",FACE,{"disambiguationData":[OSD([sQuery(id+"F2.wireOp",EDGE,"E10")])]});Q7=makeQuery(id+"F10.boolean.opBoolean","INTERSECT",EDGE,{"derivedFrom":[makeQuery(id+"F6.boolean.opBoolean","SPLIT",FACE,{"disambiguationData":[TD([subQ19,subQ20,subQ21,subQ22,subQ17,subQ15,subQ13,subQ11,subQ9,subQ4,subQ23,subQ24,subQ25,subQ18,subQ26,subQ27,makeQuery(id+"F6.opRevolve","SWEPT_FACE",FACE,{"disambiguationData":[OSD([sQuery(id+"F2.wireOp",EDGE,"E11")])]})])],"derivedFrom":makeQuery(id+"F5.boolean.opBoolean","SPLIT",FACE,{"disambiguationData":[TD([subQ19,subQ20,subQ21,subQ22,subQ17,subQ15,subQ13,subQ11,subQ9,subQ4,subQ23,subQ24,subQ25,subQ18,subQ26,subQ27])],"derivedFrom":makeQuery(id+"F4.boolean.opBoolean","SPLIT",FACE,{"disambiguationData":[TD([subQ19,subQ20,subQ21,subQ22,subQ17,subQ15,subQ13,subQ11,subQ9,subQ4,subQ23,subQ24,subQ25,subQ18,subQ26])],"derivedFrom":makeQuery(id+"F3.boolean.opBoolean","SPLIT",FACE,{"disambiguationData":[TD([subQ19,subQ20,subQ21,subQ22,subQ17,subQ15,subQ13,subQ11,subQ9,subQ4,subQ23,subQ24,subQ25,subQ18])],"derivedFrom":subQ20})})})}),makeQuery(id+"F10.opExtrude","SWEPT_FACE",FACE,{"disambiguationData":[OSD([subQ0])]})]});}
            fillet(context, id + "F11", {"entities" : qUnion([Q0, Q1, Q2, Q3, Q4, Q5, Q6, Q7]), "radius" : 1 * mm, "tangentPropagation" : true, "allowEdgeOverflow" : false});
        }
    });
